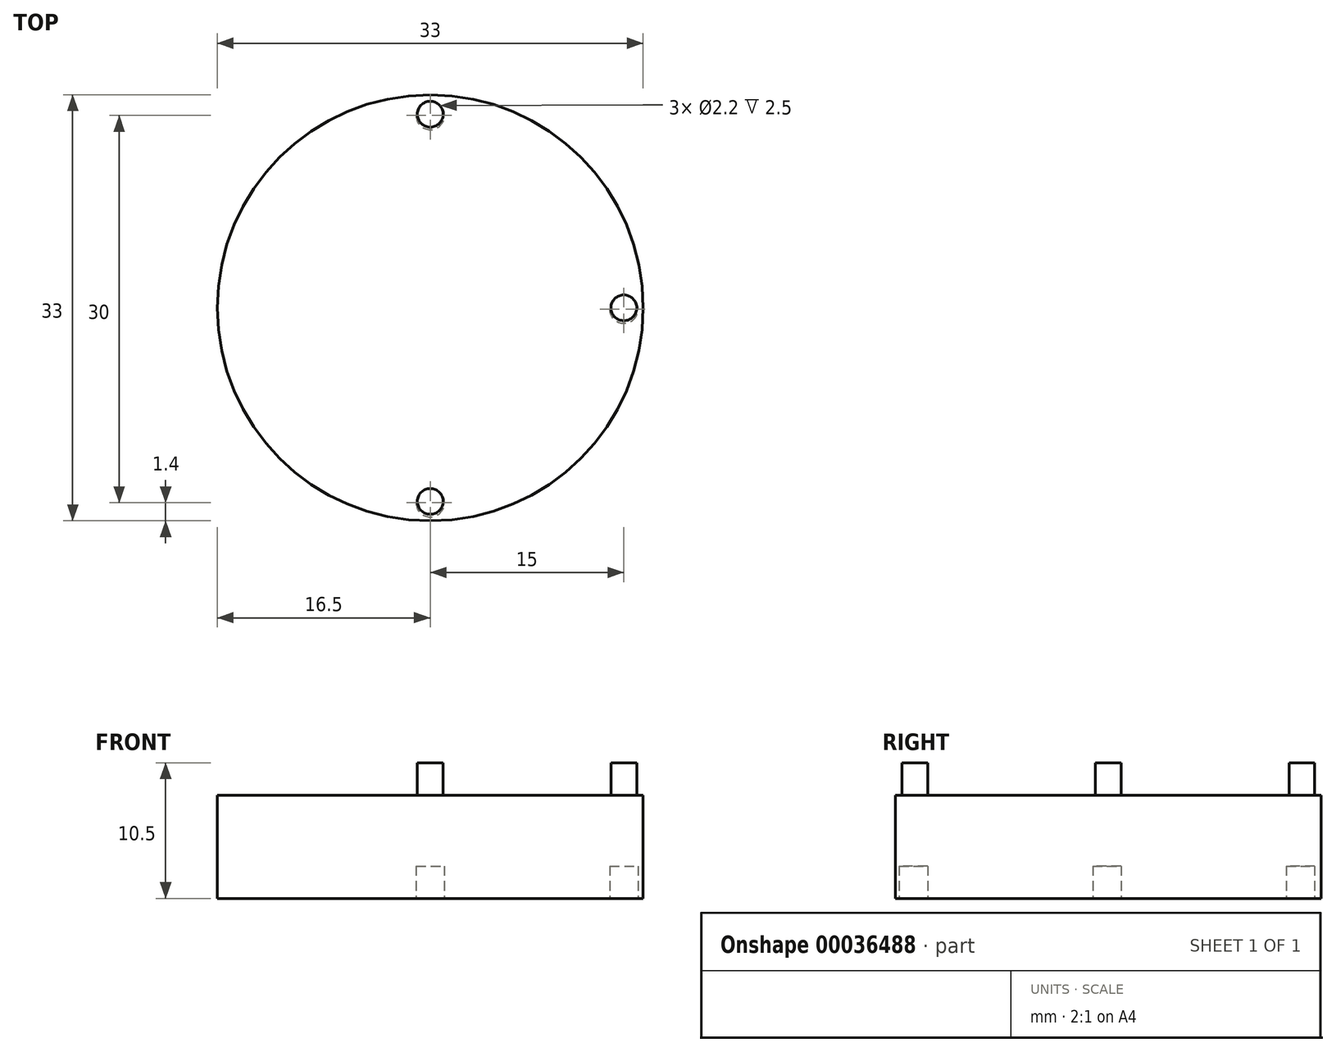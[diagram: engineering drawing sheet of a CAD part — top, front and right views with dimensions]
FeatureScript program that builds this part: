
annotation { "Feature Type Name" : "Feature", "Feature Type Description" : "" }
export const myFeature = defineFeature(function(context is Context, id is Id, definition is map)
    precondition{}
    {
        {
            var Q0;
            Q0=qCreatedBy(makeId("Top.planeOp"),FACE);
            var sketch = newSketch(context, id + "F0", { "sketchPlane" : qUnion([Q0])});
            skCircle(sketch, "E0", {"center": v(0, 0) * mm, "radius": 16.5 * mm});
            skSolve(sketch);
        }
        {
            var Q0;
            Q0 = qSketchRegion(id + "F0", true);
            extrude(context, id + "F1", {"entities" : qUnion([Q0]), "depth" : 8 * mm});
        }
        {
            var Q0;
            Q0=makeQuery(id+"F1.opExtrude","CAP_FACE",FACE,{"disambiguationData":[OSD([sQuery(id+"F0.wireOp",EDGE,"E0")])],"isStart":true});
            var sketch = newSketch(context, id + "F2", { "sketchPlane" : qUnion([Q0])});
            skCircle(sketch, "E1", {"center": v(0, 15.1) * mm, "radius": 1.1 * mm});
            skCircle(sketch, "E2.1.0", {"center": v(15, 0.1) * mm, "radius": 1.1 * mm});
            skCircle(sketch, "E2.2.0", {"center": v(0, -14.9) * mm, "radius": 1.1 * mm});
            skPoint(sketch, "E2.center", {"position": v(0, 0.1) * mm});
            skLineSegment(sketch, "E2.anchor1", {"start": v(0, 0.1) * mm, "end": v(0, 15.1) * mm, "construction": true});
            skLineSegment(sketch, "E2.anchor2", {"start": v(0, 0.1) * mm, "end": v(0, -14.9) * mm, "construction": true});
            skSolve(sketch);
        }
        {
            var Q0;
            Q0 = qSketchRegion(id + "F2", true);
            extrude(context, id + "F3", {"entities" : qUnion([Q0]), "operationType" : NewBodyOperationType.REMOVE, "oppositeDirection" : true, "depth" : 2.5 * mm});
        }
        {
            var Q0;
            Q0=makeQuery(id+"F1.opExtrude","CAP_FACE",FACE,{"disambiguationData":[OSD([sQuery(id+"F0.wireOp",EDGE,"E0")])],"isStart":false});
            var sketch = newSketch(context, id + "F4", { "sketchPlane" : qUnion([Q0])});
            skCircle(sketch, "E3", {"center": v(0, 15) * mm, "radius": 1 * mm});
            skCircle(sketch, "E4.1.0", {"center": v(15, 0) * mm, "radius": 1 * mm});
            skCircle(sketch, "E4.2.0", {"center": v(0, -15) * mm, "radius": 1 * mm});
            skPoint(sketch, "E4.center", {"position": v(0, 0) * mm});
            skLineSegment(sketch, "E4.anchor1", {"start": v(0, 0) * mm, "end": v(0, 15) * mm, "construction": true});
            skLineSegment(sketch, "E4.anchor2", {"start": v(0, 0) * mm, "end": v(0, -15) * mm, "construction": true});
            skSolve(sketch);
        }
        {
            var Q0;
            Q0 = qSketchRegion(id + "F4", true);
            extrude(context, id + "F5", {"entities" : qUnion([Q0]), "operationType" : NewBodyOperationType.ADD, "depth" : 2.5 * mm});
        }
    });
